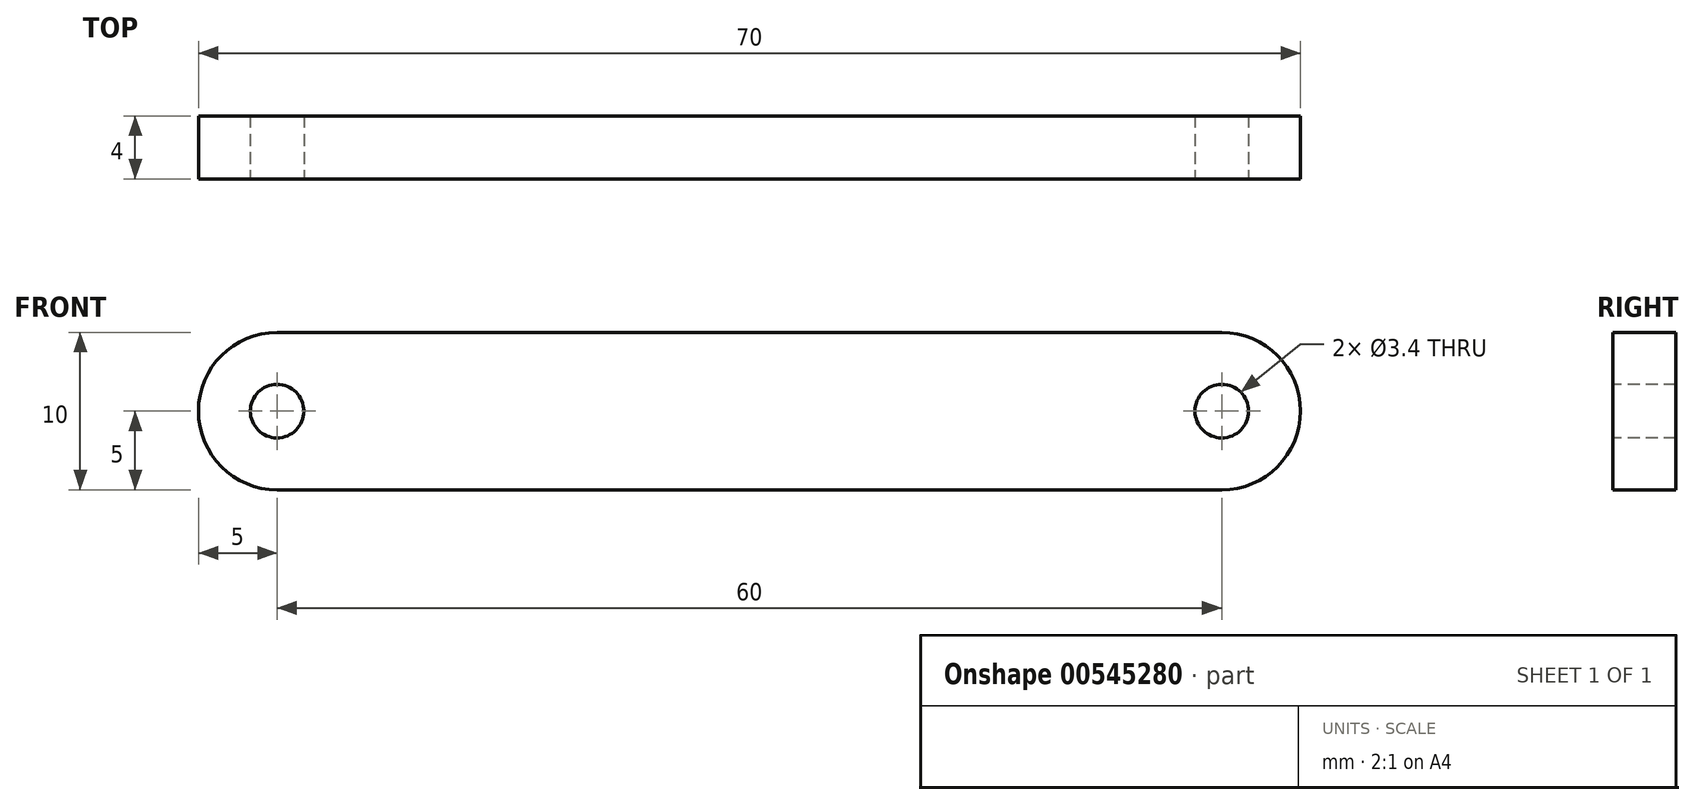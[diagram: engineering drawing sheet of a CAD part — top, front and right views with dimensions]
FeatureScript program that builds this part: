
annotation { "Feature Type Name" : "Feature", "Feature Type Description" : "" }
export const myFeature = defineFeature(function(context is Context, id is Id, definition is map)
    precondition{}
    {
        {
            var Q0;
            Q0=qCreatedBy(makeId("Front.planeOp"),FACE);
            var sketch = newSketch(context, id + "F0", { "sketchPlane" : qUnion([Q0])});
            skLineSegment(sketch, "E0", {"start": v(0, 5) * mm, "end": v(60, 5) * mm});
            skLineSegment(sketch, "E1", {"start": v(0, -5) * mm, "end": v(60, -5) * mm});
            skArc(sketch, "E2", {"start": v(0, 5) * mm, "mid": v(-5, 0) * mm, "end": v(0, -5) * mm});
            skArc(sketch, "E3", {"start": v(60, -5) * mm, "mid": v(65, 0) * mm, "end": v(60, 5) * mm});
            skSolve(sketch);
        }
        {
            var Q0;
            Q0 = qSketchRegion(id + "F0", true);
            extrude(context, id + "F1", {"entities" : qUnion([Q0]), "depth" : 4 * mm, "offsetDistance" : 25 * mm});
        }
        {
            var Q0;
            Q0=sQuery(id+"F0.wireOp",VERTEX,"E2.center");
            var Q1;
            Q1=sQuery(id+"F0.wireOp",VERTEX,"E3.center");
            var Q2;
            Q2=makeQuery(id+"F1.opExtrude","SWEPT_BODY",BODY,{"disambiguationData":[OSD([sQuery(id+"F0.wireOp",EDGE,"E0"),sQuery(id+"F0.wireOp",EDGE,"E1"),sQuery(id+"F0.wireOp",EDGE,"E2"),sQuery(id+"F0.wireOp",EDGE,"E3")])]});
            hole(context, id + "F2", {"style" : HoleStyle.SIMPLE, "endStyle" : HoleEndStyle.THROUGH, "oppositeDirection" : true, "standardTappedOrClearance" : lookupTablePath({ "fit" : "Normal", "standard" : "ISO", "size" : "M3", "type" : "Clearance" }), "standardBlindInLast" : lookupTablePath({ "fit" : "Normal", "standard" : "ISO", "engagement" : "75%", "pitch" : "0.5 mm", "size" : "M3", "type" : "Clearance & tapped" }), "holeDiameter" : 3.4 * mm, "majorDiameter" : 5 * mm, "isTappedThrough" : true, "tappedDepth" : 12 * mm, "tapClearance" : 3, "locations" : qUnion([Q0, Q1]), "scope" : qUnion([Q2]), "startStyle" : HoleStartStyle.PART});
        }
    });
